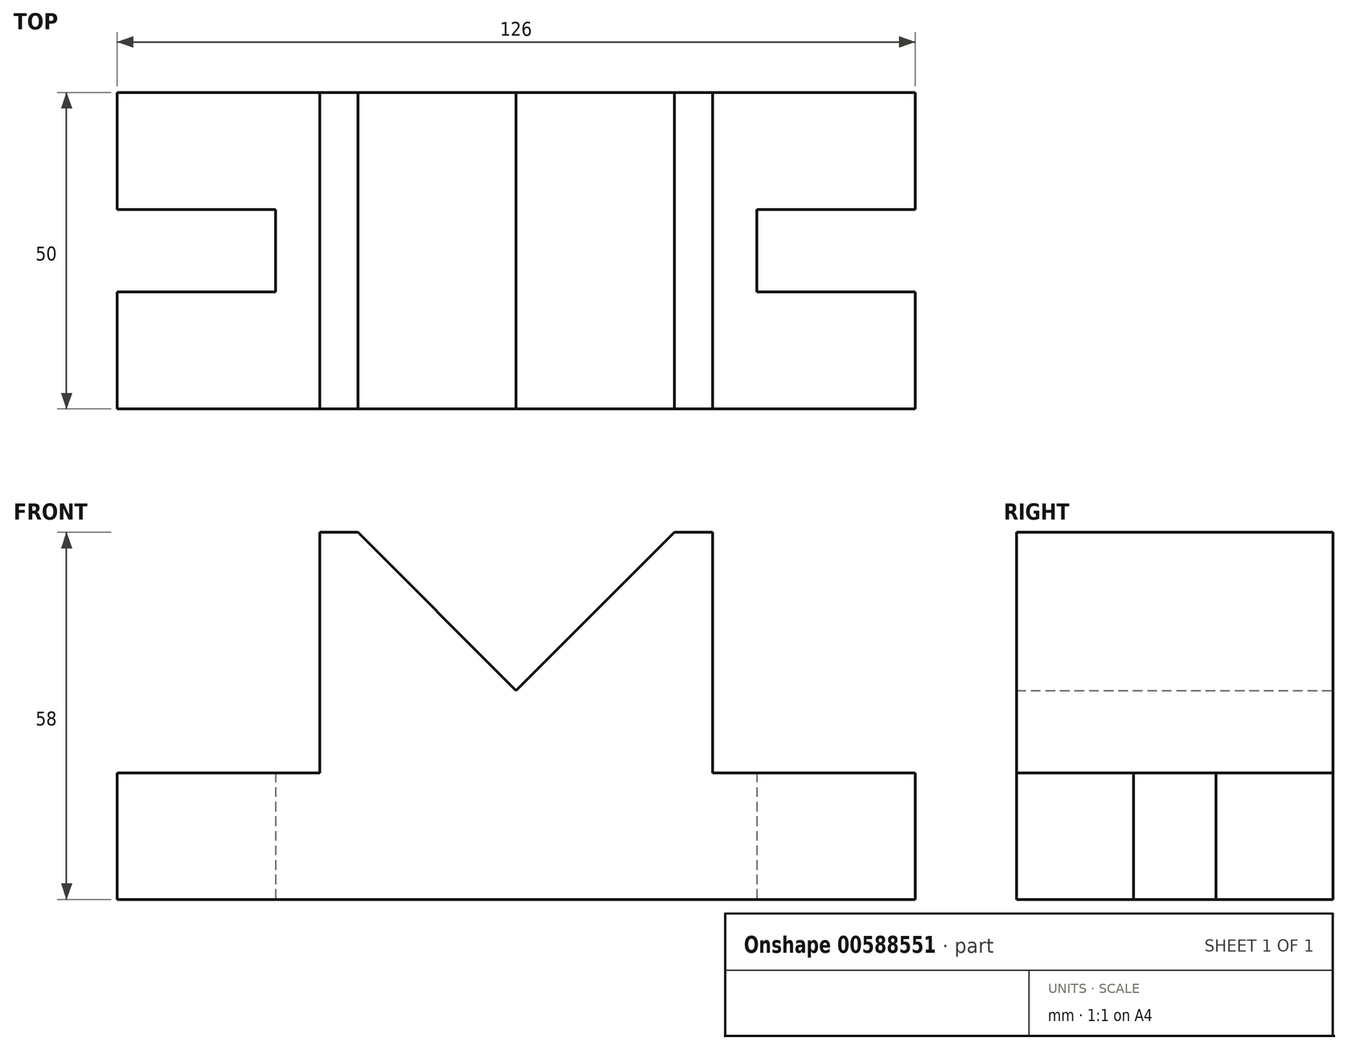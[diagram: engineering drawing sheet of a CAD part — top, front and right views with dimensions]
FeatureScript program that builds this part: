
annotation { "Feature Type Name" : "Feature", "Feature Type Description" : "" }
export const myFeature = defineFeature(function(context is Context, id is Id, definition is map)
    precondition{}
    {
        {
            var Q0;
            Q0=qCreatedBy(makeId("Front.planeOp"),FACE);
            var sketch = newSketch(context, id + "F0", { "sketchPlane" : qUnion([Q0])});
            skLineSegment(sketch, "E0", {"start": v(0, 0) * mm, "end": v(63, 0) * mm});
            skLineSegment(sketch, "E1", {"start": v(63, 0) * mm, "end": v(63, 20) * mm});
            skLineSegment(sketch, "E2", {"start": v(63, 20) * mm, "end": v(31, 20) * mm});
            skLineSegment(sketch, "E3", {"start": v(31, 20) * mm, "end": v(31, 58) * mm});
            skLineSegment(sketch, "E4", {"start": v(31, 58) * mm, "end": v(25, 58) * mm});
            skLineSegment(sketch, "E5", {"start": v(25, 58) * mm, "end": v(0, 33) * mm});
            skLineSegment(sketch, "E6", {"start": v(0, 33) * mm, "end": v(0, 0) * mm});
            skSolve(sketch);
        }
        {
            var Q0;
            Q0=makeQuery(id+"F0.imprint","IMPRINT",FACE,{"disambiguationData":[TD([[makeQuery(id+"F0.imprint","IMPRINT",EDGE,{"derivedFrom":sQuery(id+"F0.wireOp",EDGE,"E0")}),1.0]])]});
            extrude(context, id + "F1", {"entities" : qUnion([Q0]), "endBound" : BoundingType.SYMMETRIC, "depth" : 50 * mm, "offsetDistance" : 25 * mm});
        }
        {
            var Q0;
            Q0=qCreatedBy(makeId("Front.planeOp"),FACE);
            var sketch = newSketch(context, id + "F2", { "sketchPlane" : qUnion([Q0])});
            skLineSegment(sketch, "E7.bottom", {"start": v(38, 34.87) * mm, "end": v(69.58, 34.87) * mm});
            skLineSegment(sketch, "E7.top", {"start": v(38, -13.1) * mm, "end": v(69.58, -13.1) * mm});
            skLineSegment(sketch, "E7.left", {"start": v(38, 34.87) * mm, "end": v(38, -13.1) * mm});
            skLineSegment(sketch, "E7.right", {"start": v(69.58, 34.87) * mm, "end": v(69.58, -13.1) * mm});
            skSolve(sketch);
        }
        {
            var Q0;
            Q0=makeQuery(id+"F2.imprint","IMPRINT",FACE,{"disambiguationData":[TD([[makeQuery(id+"F2.imprint","IMPRINT",EDGE,{"derivedFrom":sQuery(id+"F2.wireOp",EDGE,"E7.bottom")}),-1.0]])]});
            extrude(context, id + "F3", {"entities" : qUnion([Q0]), "operationType" : NewBodyOperationType.REMOVE, "endBound" : BoundingType.SYMMETRIC, "oppositeDirection" : true, "depth" : 13 * mm, "offsetDistance" : 25 * mm});
        }
        {
            var Q0;
            Q0=makeQuery(id+"F1.opExtrude","SWEPT_BODY",BODY,{"disambiguationData":[OSD([sQuery(id+"F0.wireOp",EDGE,"E0"),sQuery(id+"F0.wireOp",EDGE,"E1"),sQuery(id+"F0.wireOp",EDGE,"E2"),sQuery(id+"F0.wireOp",EDGE,"E3"),sQuery(id+"F0.wireOp",EDGE,"E4"),sQuery(id+"F0.wireOp",EDGE,"E5"),sQuery(id+"F0.wireOp",EDGE,"E6")])]});
            var Q1;
            Q1=qCreatedBy(makeId("Right.planeOp"),FACE);
            mirror(context, id + "F4", {"operationType" : NewBodyOperationType.ADD, "entities" : qUnion([Q0]), "mirrorPlane" : qUnion([Q1])});
        }
    });
